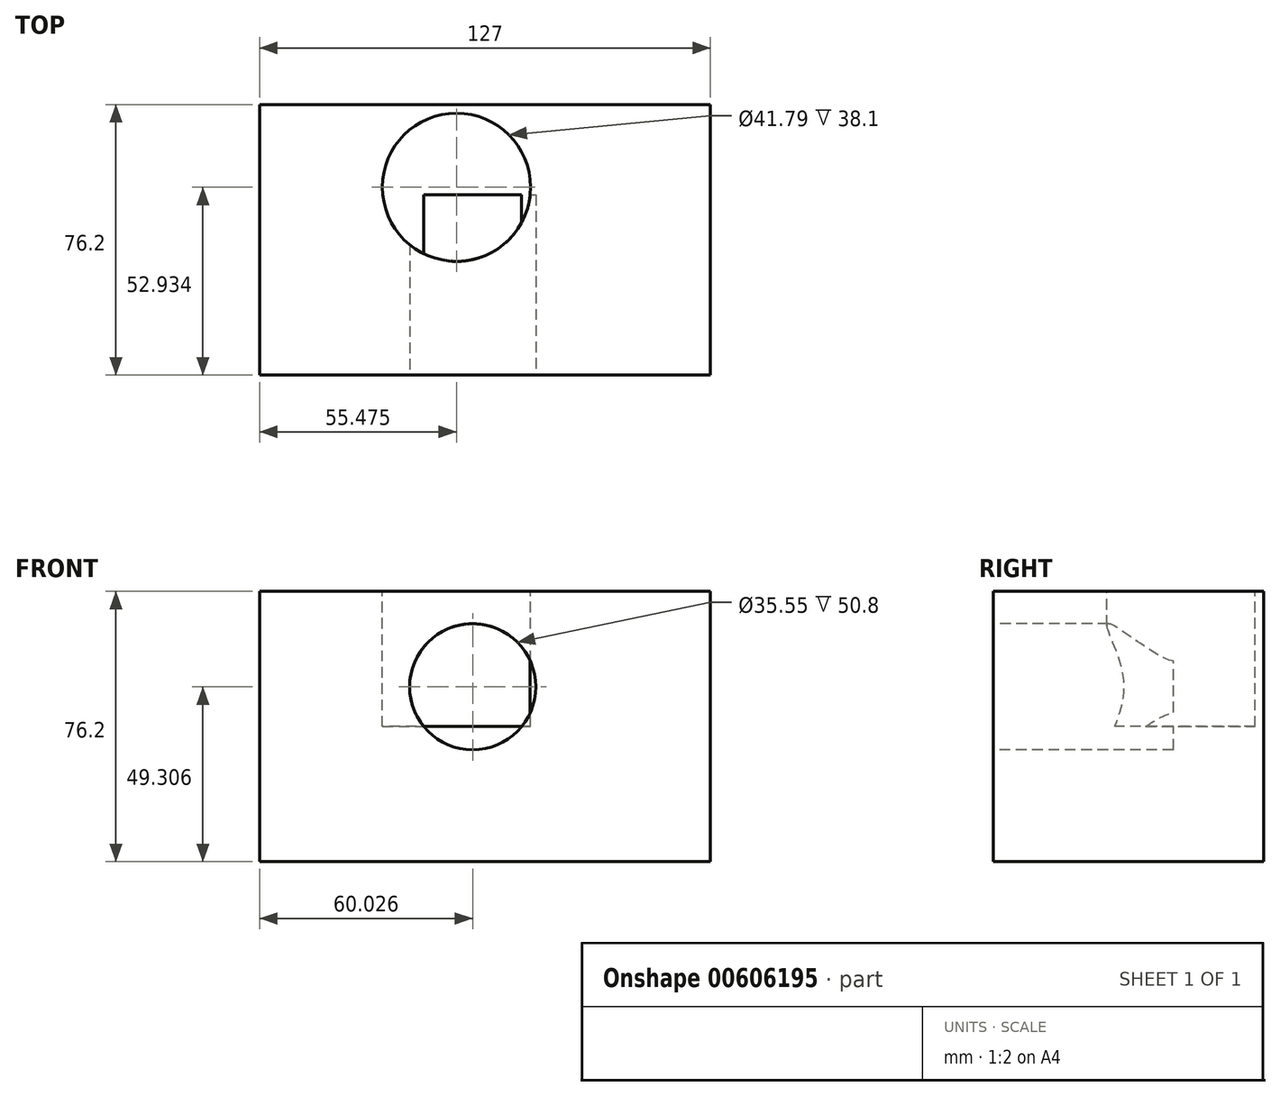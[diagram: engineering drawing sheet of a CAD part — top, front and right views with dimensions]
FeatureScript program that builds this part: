
annotation { "Feature Type Name" : "Feature", "Feature Type Description" : "" }
export const myFeature = defineFeature(function(context is Context, id is Id, definition is map)
    precondition{}
    {
        {
            var Q0;
            Q0=qCreatedBy(makeId("Front.planeOp"),FACE);
            var sketch = newSketch(context, id + "F0", { "sketchPlane" : qUnion([Q0])});
            skLineSegment(sketch, "E0.bottom", {"start": v(-81.82, 76.2) * mm, "end": v(45.18, 76.2) * mm});
            skLineSegment(sketch, "E0.top", {"start": v(-81.82, 0) * mm, "end": v(45.18, 0) * mm});
            skLineSegment(sketch, "E0.left", {"start": v(-81.82, 76.2) * mm, "end": v(-81.82, 0) * mm});
            skLineSegment(sketch, "E0.right", {"start": v(45.18, 76.2) * mm, "end": v(45.18, 0) * mm});
            skSolve(sketch);
        }
        {
            var Q0;
            Q0=makeQuery(id+"F0.imprint","IMPRINT",FACE,{"disambiguationData":[TD([[makeQuery(id+"F0.imprint","IMPRINT",EDGE,{"derivedFrom":sQuery(id+"F0.wireOp",EDGE,"E0.bottom")}),-1.0]])]});
            extrude(context, id + "F1", {"entities" : qUnion([Q0]), "depth" : 76.2 * mm, "offsetDistance" : 25.4 * mm});
        }
        {
            var Q0;
            Q0=makeQuery(id+"F1.opExtrude","SWEPT_FACE",FACE,{"disambiguationData":[OSD([sQuery(id+"F0.wireOp",EDGE,"E0.bottom")])]});
            var sketch = newSketch(context, id + "F2", { "sketchPlane" : qUnion([Q0])});
            skCircle(sketch, "E1", {"center": v(-26.34, -23.27) * mm, "radius": 20.9 * mm});
            skSolve(sketch);
        }
        {
            var Q0;
            Q0=makeQuery(id+"F2.imprint","IMPRINT",FACE,{"disambiguationData":[TD([[makeQuery(id+"F2.imprint","IMPRINT",EDGE,{"derivedFrom":sQuery(id+"F2.wireOp",EDGE,"E1")}),1.0]])]});
            extrude(context, id + "F3", {"entities" : qUnion([Q0]), "operationType" : NewBodyOperationType.REMOVE, "oppositeDirection" : true, "depth" : 38.1 * mm, "offsetDistance" : 25.4 * mm});
        }
        {
            var Q0;
            Q0=makeQuery(id+"F1.opExtrude","CAP_FACE",FACE,{"disambiguationData":[OSD([sQuery(id+"F0.wireOp",EDGE,"E0.bottom"),sQuery(id+"F0.wireOp",EDGE,"E0.top"),sQuery(id+"F0.wireOp",EDGE,"E0.left"),sQuery(id+"F0.wireOp",EDGE,"E0.right")])],"isStart":false});
            var sketch = newSketch(context, id + "F4", { "sketchPlane" : qUnion([Q0])});
            skCircle(sketch, "E2", {"center": v(-21.8, 49.3) * mm, "radius": 17.77 * mm});
            skSolve(sketch);
        }
        {
            var Q0;
            Q0=makeQuery(id+"F4.imprint","IMPRINT",FACE,{"disambiguationData":[TD([[makeQuery(id+"F4.imprint","IMPRINT",EDGE,{"derivedFrom":sQuery(id+"F4.wireOp",EDGE,"E2")}),1.0]])]});
            extrude(context, id + "F5", {"entities" : qUnion([Q0]), "operationType" : NewBodyOperationType.REMOVE, "oppositeDirection" : true, "depth" : 50.8 * mm, "offsetDistance" : 25.4 * mm});
        }
    });
